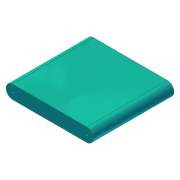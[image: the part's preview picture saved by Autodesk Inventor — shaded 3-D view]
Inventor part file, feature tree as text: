
AUTODESK INVENTOR PART (.ipt)
format: ipt  version: 2012 (Build 160160000, 160)  size: 84,992 bytes
history: native  units: in
note: dims shown in document units (in); Inventor stores cm internally (conversion verified against a paired STEP export)
features: extrude x2, sketch x2
ambient origin geometry x8: Origin, YZ Plane, XZ Plane, XY Plane, X Axis, Y Axis, Z Axis, Center Point
bodies: Solid1 (feature_tree)
feature tree (4):
  extrude  "Extrusion1"  Depth=11.0in
  extrude  "Extrusion2"  Depth=0.375in
  sketch  "Sketch1"  dims[d0=1.0in d1=11.0in]
  sketch  "Sketch2"  dims[d2=10.0in d3=0.0in d4=0.375in d5=1.0in d6=0.0in]
